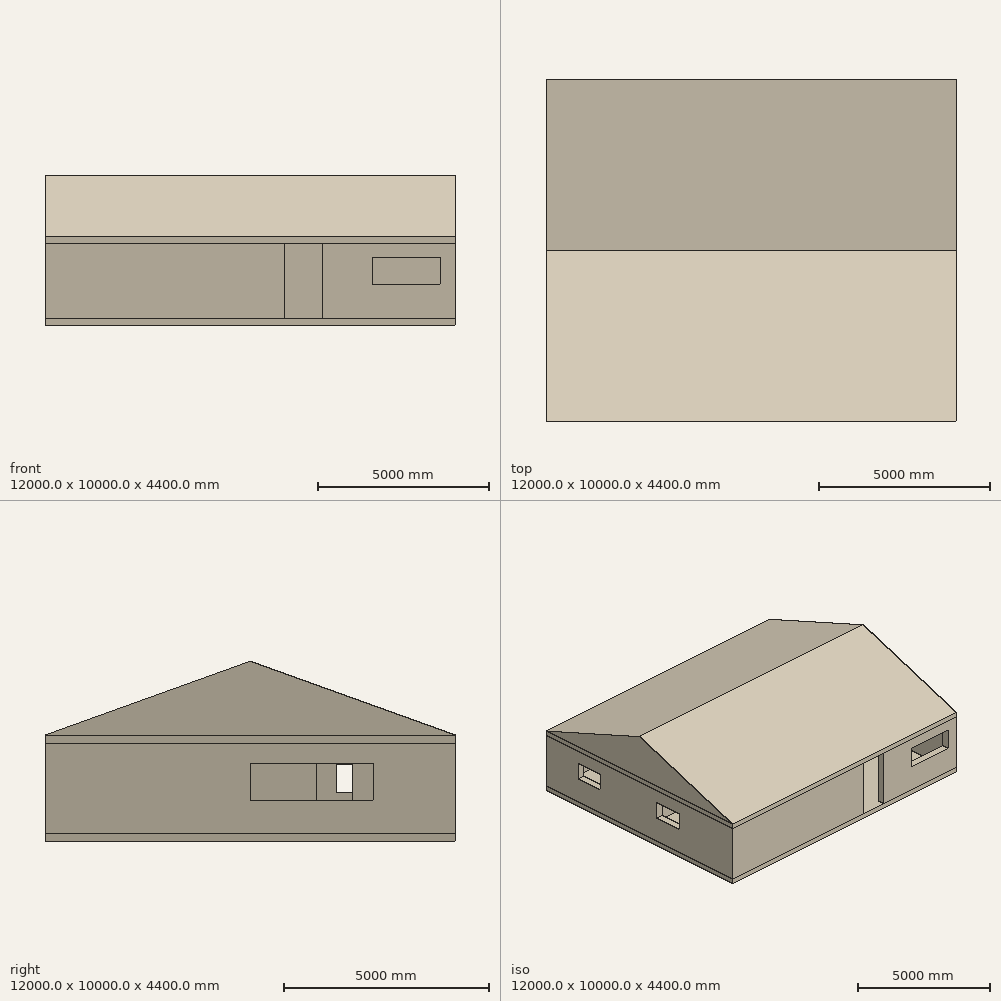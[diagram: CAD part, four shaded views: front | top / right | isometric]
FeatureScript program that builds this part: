
annotation { "Feature Type Name" : "Feature", "Feature Type Description" : "" }
export const myFeature = defineFeature(function(context is Context, id is Id, definition is map)
    precondition{}
    {
        {
            var Q0;
            Q0=qCreatedBy(makeId("Top.planeOp"),FACE);
            var sketch = newSketch(context, id + "F0", { "sketchPlane" : qUnion([Q0])});
            skLineSegment(sketch, "E0.bottom", {"start": v(0, 0) * mm, "end": v(7000, 0) * mm});
            skLineSegment(sketch, "E0.top", {"start": v(0, 10000) * mm, "end": v(12000, 10000) * mm});
            skLineSegment(sketch, "E0.left", {"start": v(0, 0) * mm, "end": v(0, 10000) * mm});
            skLineSegment(sketch, "E0.right", {"start": v(12000, 0) * mm, "end": v(12000, 10000) * mm});
            skLineSegment(sketch, "E1.0", {"start": v(300, 300) * mm, "end": v(300, 5100) * mm});
            skLineSegment(sketch, "E1.1", {"start": v(300, 300) * mm, "end": v(5400, 300) * mm});
            skLineSegment(sketch, "E1.2", {"start": v(11700, 300) * mm, "end": v(11700, 9700) * mm});
            skLineSegment(sketch, "E1.3", {"start": v(300, 9700) * mm, "end": v(5400, 9700) * mm});
            skLineSegment(sketch, "E2", {"start": v(7000, 300) * mm, "end": v(7000, 0) * mm});
            skLineSegment(sketch, "E3", {"start": v(8100, 300) * mm, "end": v(8100, 0) * mm});
            skLineSegment(sketch, "E4.trimOffspring", {"start": v(8100, 300) * mm, "end": v(11700, 300) * mm});
            skLineSegment(sketch, "E5.trimOffspring", {"start": v(8100, 0) * mm, "end": v(12000, 0) * mm});
            skLineSegment(sketch, "E6", {"start": v(5600, 300) * mm, "end": v(5600, 9700) * mm});
            skLineSegment(sketch, "E7.0", {"start": v(5400, 300) * mm, "end": v(5400, 5100) * mm});
            skLineSegment(sketch, "E8", {"start": v(300, 5300) * mm, "end": v(5400, 5300) * mm});
            skLineSegment(sketch, "E9.0", {"start": v(300, 5100) * mm, "end": v(5400, 5100) * mm});
            skLineSegment(sketch, "E10.trimOffspring", {"start": v(5400, 5300) * mm, "end": v(5400, 9700) * mm});
            skLineSegment(sketch, "E11.trimOffspring", {"start": v(300, 5300) * mm, "end": v(300, 9700) * mm});
            skLineSegment(sketch, "E12.trimOffspring", {"start": v(5600, 9700) * mm, "end": v(11700, 9700) * mm});
            skLineSegment(sketch, "E13.trimOffspring", {"start": v(5600, 300) * mm, "end": v(7000, 300) * mm});
            skSolve(sketch);
        }
        {
            var Q0;
            Q0=makeQuery(id+"F0.imprint","IMPRINT",FACE,{"disambiguationData":[TD([[makeQuery(id+"F0.imprint","IMPRINT",EDGE,{"derivedFrom":sQuery(id+"F0.wireOp",EDGE,"E0.bottom")}),1.0]])]});
            extrude(context, id + "F1", {"entities" : qUnion([Q0]), "depth" : 2200 * mm});
        }
        {
            var Q0;
            Q0=makeQuery(id+"F1.opExtrude","SWEPT_FACE",FACE,{"disambiguationData":[OSD([sQuery(id+"F0.wireOp",EDGE,"E0.left")])]});
            var sketch = newSketch(context, id + "F2", { "sketchPlane" : qUnion([Q0])});
            skLineSegment(sketch, "E14.bottom", {"start": v(-8293.38, 1680) * mm, "end": v(-7093.38, 1680) * mm});
            skLineSegment(sketch, "E14.top", {"start": v(-8293.38, 1000) * mm, "end": v(-7093.38, 1000) * mm});
            skLineSegment(sketch, "E14.left", {"start": v(-8293.38, 1680) * mm, "end": v(-8293.38, 1000) * mm});
            skLineSegment(sketch, "E14.right", {"start": v(-7093.38, 1680) * mm, "end": v(-7093.38, 1000) * mm});
            skLineSegment(sketch, "E15.bottom", {"start": v(-4078.06, 1680) * mm, "end": v(-2878.06, 1680) * mm});
            skLineSegment(sketch, "E15.top", {"start": v(-4078.06, 1000) * mm, "end": v(-2878.06, 1000) * mm});
            skLineSegment(sketch, "E15.left", {"start": v(-4078.06, 1680) * mm, "end": v(-4078.06, 1000) * mm});
            skLineSegment(sketch, "E15.right", {"start": v(-2878.06, 1680) * mm, "end": v(-2878.06, 1000) * mm});
            skSolve(sketch);
        }
        {
            var Q0;
            Q0=qSketchRegion(id+"F2",true);
            extrude(context, id + "F3", {"entities" : qUnion([Q0]), "operationType" : NewBodyOperationType.REMOVE, "endBound" : BoundingType.UP_TO_NEXT, "oppositeDirection" : true, "depth" : 25 * mm});
        }
        {
            var Q0;
            Q0=makeQuery(id+"F1.opExtrude","SWEPT_FACE",FACE,{"disambiguationData":[OSD([sQuery(id+"F0.wireOp",EDGE,"E6")])]});
            var sketch = newSketch(context, id + "F4", { "sketchPlane" : qUnion([Q0])});
            skLineSegment(sketch, "E16.bottom", {"start": v(6600, 0) * mm, "end": v(7500, 0) * mm});
            skLineSegment(sketch, "E16.top", {"start": v(6600, 1900) * mm, "end": v(7500, 1900) * mm});
            skLineSegment(sketch, "E16.left", {"start": v(6600, 0) * mm, "end": v(6600, 1900) * mm});
            skLineSegment(sketch, "E16.right", {"start": v(7500, 0) * mm, "end": v(7500, 1900) * mm});
            skLineSegment(sketch, "E17.bottom", {"start": v(1900, 0) * mm, "end": v(2800, 0) * mm});
            skLineSegment(sketch, "E17.top", {"start": v(1900, 1900) * mm, "end": v(2800, 1900) * mm});
            skLineSegment(sketch, "E17.left", {"start": v(1900, 0) * mm, "end": v(1900, 1900) * mm});
            skLineSegment(sketch, "E17.right", {"start": v(2800, 0) * mm, "end": v(2800, 1900) * mm});
            skSolve(sketch);
        }
        {
            var Q0;
            Q0=qSketchRegion(id+"F4",true);
            extrude(context, id + "F5", {"entities" : qUnion([Q0]), "operationType" : NewBodyOperationType.REMOVE, "endBound" : BoundingType.UP_TO_NEXT, "oppositeDirection" : true, "depth" : 25 * mm});
        }
        {
            var Q0;
            Q0=makeQuery(id+"F1.opExtrude","SWEPT_FACE",FACE,{"disambiguationData":[OSD([sQuery(id+"F0.wireOp",EDGE,"E5.trimOffspring")])]});
            var sketch = newSketch(context, id + "F6", { "sketchPlane" : qUnion([Q0])});
            skLineSegment(sketch, "E18.bottom", {"start": v(9562.96, 1000) * mm, "end": v(11562.96, 1000) * mm});
            skLineSegment(sketch, "E18.top", {"start": v(9562.96, 1800) * mm, "end": v(11562.96, 1800) * mm});
            skLineSegment(sketch, "E18.left", {"start": v(9562.96, 1000) * mm, "end": v(9562.96, 1800) * mm});
            skLineSegment(sketch, "E18.right", {"start": v(11562.96, 1000) * mm, "end": v(11562.96, 1800) * mm});
            skSolve(sketch);
        }
        {
            var Q0;
            Q0=makeQuery(id+"F6.imprint","IMPRINT",FACE,{"disambiguationData":[TD([[makeQuery(id+"F6.imprint","IMPRINT",EDGE,{"derivedFrom":sQuery(id+"F6.wireOp",EDGE,"E18.bottom")}),1.0]])]});
            var Q1;
            Q1=sQuery(id+"F6.wireOp",EDGE,"E18.bottom");
            var Q2;
            Q2=sQuery(id+"F6.wireOp",EDGE,"E18.top");
            var Q3;
            Q3=sQuery(id+"F6.wireOp",EDGE,"E18.left");
            var Q4;
            Q4=sQuery(id+"F6.wireOp",EDGE,"E18.right");
            extrude(context, id + "F7", {"entities" : qUnion([Q0]), "operationType" : NewBodyOperationType.REMOVE, "surfaceEntities" : qUnion([Q1, Q2, Q3, Q4]), "endBound" : BoundingType.UP_TO_NEXT, "oppositeDirection" : true, "depth" : 25 * mm});
        }
        {
            var Q0;
            Q0=makeQuery(id+"F1.opExtrude","CAP_FACE",FACE,{"disambiguationData":[OSD([sQuery(id+"F0.wireOp",EDGE,"E0.bottom"),sQuery(id+"F0.wireOp",EDGE,"E0.top"),sQuery(id+"F0.wireOp",EDGE,"E0.left"),sQuery(id+"F0.wireOp",EDGE,"E0.right"),sQuery(id+"F0.wireOp",EDGE,"E1.0"),sQuery(id+"F0.wireOp",EDGE,"E1.1"),sQuery(id+"F0.wireOp",EDGE,"E1.2"),sQuery(id+"F0.wireOp",EDGE,"E1.3"),sQuery(id+"F0.wireOp",EDGE,"E2"),sQuery(id+"F0.wireOp",EDGE,"E3"),sQuery(id+"F0.wireOp",EDGE,"E4.trimOffspring"),sQuery(id+"F0.wireOp",EDGE,"E5.trimOffspring"),sQuery(id+"F0.wireOp",EDGE,"E6"),sQuery(id+"F0.wireOp",EDGE,"E7.0"),sQuery(id+"F0.wireOp",EDGE,"E8"),sQuery(id+"F0.wireOp",EDGE,"E9.0"),sQuery(id+"F0.wireOp",EDGE,"E10.trimOffspring"),sQuery(id+"F0.wireOp",EDGE,"E11.trimOffspring"),sQuery(id+"F0.wireOp",EDGE,"E12.trimOffspring"),sQuery(id+"F0.wireOp",EDGE,"E13.trimOffspring")])],"isStart":true});
            var sketch = newSketch(context, id + "F8", { "sketchPlane" : qUnion([Q0])});
            skLineSegment(sketch, "E19.0", {"start": v(0, 0) * mm, "end": v(0, -10000) * mm});
            skLineSegment(sketch, "E20.0", {"start": v(0, 0) * mm, "end": v(12000, 0) * mm});
            skLineSegment(sketch, "E21.0", {"start": v(12000, 0) * mm, "end": v(12000, -10000) * mm});
            skLineSegment(sketch, "E22.0", {"start": v(0, -10000) * mm, "end": v(12000, -10000) * mm});
            skSolve(sketch);
        }
        {
            var Q0;
            Q0=qSketchRegion(id+"F8",true);
            extrude(context, id + "F9", {"entities" : qUnion([Q0]), "depth" : 200 * mm});
        }
        {
            var Q0;
            Q0=makeQuery(id+"F1.opExtrude","CAP_FACE",FACE,{"disambiguationData":[OSD([sQuery(id+"F0.wireOp",EDGE,"E0.bottom"),sQuery(id+"F0.wireOp",EDGE,"E0.top"),sQuery(id+"F0.wireOp",EDGE,"E0.left"),sQuery(id+"F0.wireOp",EDGE,"E0.right"),sQuery(id+"F0.wireOp",EDGE,"E1.0"),sQuery(id+"F0.wireOp",EDGE,"E1.1"),sQuery(id+"F0.wireOp",EDGE,"E1.2"),sQuery(id+"F0.wireOp",EDGE,"E1.3"),sQuery(id+"F0.wireOp",EDGE,"E2"),sQuery(id+"F0.wireOp",EDGE,"E3"),sQuery(id+"F0.wireOp",EDGE,"E4.trimOffspring"),sQuery(id+"F0.wireOp",EDGE,"E5.trimOffspring"),sQuery(id+"F0.wireOp",EDGE,"E6"),sQuery(id+"F0.wireOp",EDGE,"E7.0"),sQuery(id+"F0.wireOp",EDGE,"E8"),sQuery(id+"F0.wireOp",EDGE,"E9.0"),sQuery(id+"F0.wireOp",EDGE,"E10.trimOffspring"),sQuery(id+"F0.wireOp",EDGE,"E11.trimOffspring"),sQuery(id+"F0.wireOp",EDGE,"E12.trimOffspring"),sQuery(id+"F0.wireOp",EDGE,"E13.trimOffspring")])],"isStart":false});
            var sketch = newSketch(context, id + "F10", { "sketchPlane" : qUnion([Q0])});
            skLineSegment(sketch, "E23.0", {"start": v(0, 0) * mm, "end": v(12000, 0) * mm});
            skLineSegment(sketch, "E24.0", {"start": v(12000, 0) * mm, "end": v(12000, 10000) * mm});
            skLineSegment(sketch, "E25.0", {"start": v(0, 10000) * mm, "end": v(12000, 10000) * mm});
            skLineSegment(sketch, "E26.0", {"start": v(0, 0) * mm, "end": v(0, 10000) * mm});
            skSolve(sketch);
        }
        {
            var Q0;
            Q0=qSketchRegion(id+"F10",true);
            extrude(context, id + "F11", {"entities" : qUnion([Q0]), "depth" : 200 * mm});
        }
        {
            var Q0;
            Q0=makeQuery(id+"F1.opExtrude","SWEPT_FACE",FACE,{"disambiguationData":[OSD([sQuery(id+"F0.wireOp",EDGE,"E0.right")])]});
            var sketch = newSketch(context, id + "F12", { "sketchPlane" : qUnion([Q0])});
            skLineSegment(sketch, "E27.0", {"start": v(0, 2400) * mm, "end": v(10000, 2400) * mm});
            skLineSegment(sketch, "E28", {"start": v(0, 2400) * mm, "end": v(5000, 4200) * mm});
            skLineSegment(sketch, "E29", {"start": v(5000, 4200) * mm, "end": v(10000, 2400) * mm});
            skSolve(sketch);
        }
        {
            var Q0;
            Q0=qSketchRegion(id+"F12",true);
            var Q1;
            Q1=makeQuery(id+"F11.opExtrude","SWEPT_FACE",FACE,{"disambiguationData":[OSD([sQuery(id+"F10.wireOp",EDGE,"E26.0")])]});
            extrude(context, id + "F13", {"entities" : qUnion([Q0]), "endBound" : BoundingType.UP_TO_SURFACE, "oppositeDirection" : true, "endBoundEntityFace" : qUnion([Q1]), "depth" : 25 * mm});
        }
        {
            var Q0;
            Q0=makeQuery(id+"F13.opExtrude","SWEPT_FACE",FACE,{"disambiguationData":[OSD([sQuery(id+"F12.wireOp",EDGE,"E27.0")])]});
            shell(context, id + "F14", {"entities" : qUnion([Q0]), "thickness" : 200 * mm});
        }
        {
            var Q0;
            Q0=makeQuery(id+"F1.opExtrude","SWEPT_FACE",FACE,{"disambiguationData":[OSD([sQuery(id+"F0.wireOp",EDGE,"E0.right")])]});
            var sketch = newSketch(context, id + "F15", { "sketchPlane" : qUnion([Q0])});
            skLineSegment(sketch, "E30.bottom", {"start": v(5000, 800) * mm, "end": v(8000, 800) * mm});
            skLineSegment(sketch, "E30.top", {"start": v(5000, 1700) * mm, "end": v(8000, 1700) * mm});
            skLineSegment(sketch, "E30.left", {"start": v(5000, 800) * mm, "end": v(5000, 1700) * mm});
            skLineSegment(sketch, "E30.right", {"start": v(8000, 800) * mm, "end": v(8000, 1700) * mm});
            skSolve(sketch);
        }
        {
            var Q0;
            Q0=qSketchRegion(id+"F15",true);
            extrude(context, id + "F16", {"entities" : qUnion([Q0]), "operationType" : NewBodyOperationType.REMOVE, "endBound" : BoundingType.UP_TO_NEXT, "oppositeDirection" : true, "depth" : 25 * mm});
        }
    });
